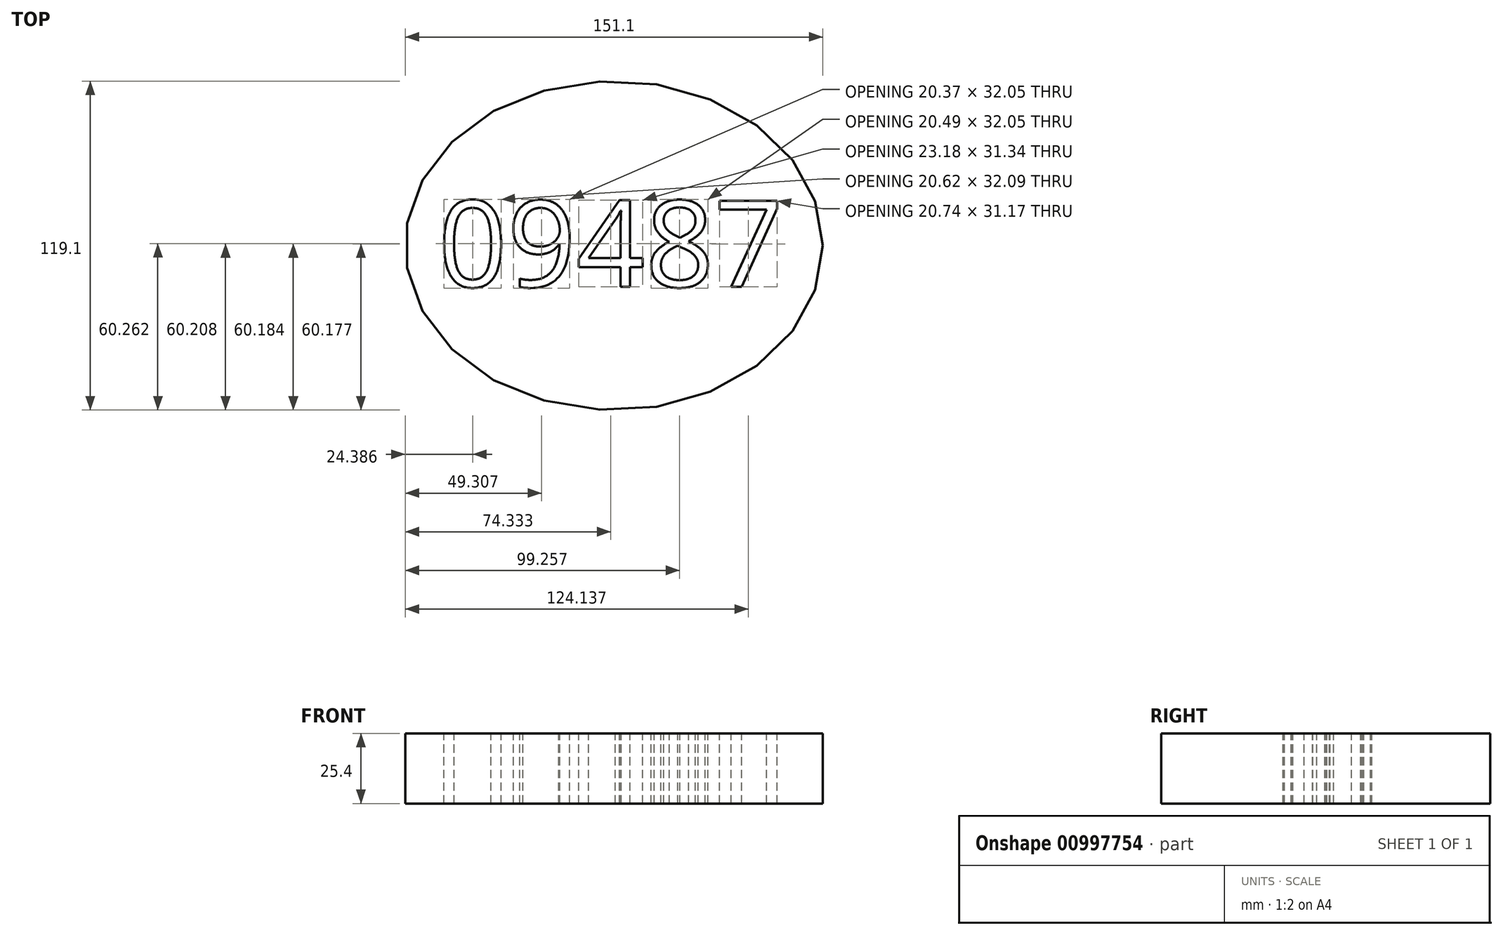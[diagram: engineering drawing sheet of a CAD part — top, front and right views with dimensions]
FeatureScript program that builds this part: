
annotation { "Feature Type Name" : "Feature", "Feature Type Description" : "" }
export const myFeature = defineFeature(function(context is Context, id is Id, definition is map)
    precondition{}
    {
        {
            var Q0;
            Q0=qCreatedBy(makeId("Top.planeOp"),FACE);
            var sketch = newSketch(context, id + "F0", { "sketchPlane" : qUnion([Q0])});
            skEllipse(sketch, "E0", {"center": v(0, -2.29) * mm, "majorRadius": 75.55 * mm, "minorRadius": 59.55 * mm, "majorAxis": v(1, 0)});
            skSolve(sketch);
        }
        {
            var Q0;
            Q0 = qSketchRegion(id + "F0", true);
            extrude(context, id + "F1", {"entities" : qUnion([Q0]), "depth" : 25.4 * mm, "offsetDistance" : 25.4 * mm});
        }
        {
            var Q0;
            Q0=makeQuery(id+"F1.opExtrude","CAP_FACE",FACE,{"disambiguationData":[OSD([sQuery(id+"F0.wireOp",EDGE,"E0")])],"isStart":false});
            var sketch = newSketch(context, id + "F2", { "sketchPlane" : qUnion([Q0])});
            skText(sketch, "E1", { "text": "09487\n", "fontName": "OpenSans-Regular.ttf"});
            const initialGuessF2  = {"E1": [-0.06365, -0.01725, 1, 0, 0.03144]};
            skSetInitialGuess(sketch, initialGuessF2);
            skSolve(sketch);
        }
        {
            var Q0;
            Q0 = qSketchRegion(id + "F2", true);
            extrude(context, id + "F3", {"entities" : qUnion([Q0]), "operationType" : NewBodyOperationType.REMOVE, "oppositeDirection" : true, "depth" : 25.4 * mm, "offsetDistance" : 25.4 * mm});
        }
    });
